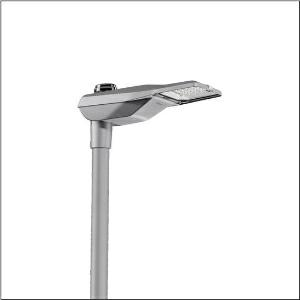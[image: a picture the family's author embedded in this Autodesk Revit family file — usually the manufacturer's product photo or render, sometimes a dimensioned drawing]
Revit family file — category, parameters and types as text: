
# Revit family: streetlight_sl_21_micro___st1_0a_5xe5d27n08db_a8cd
name_source: partatom
category: Lighting Fixtures
units: mm (PartAtom-declared; Revit-internal decimal feet)

## family parameters
Cut with Voids When Loaded = No
Host = Face
Light Source = No
Part Type = Normal
Room Calculation Point = No
Round Connector Dimension = Use Diameter
Shared = No

## types (1)
- --- (1 x LED, 4230 lm, 39.1 W, 2200K)
    Apparent Load = 39 VA
    CIE Flux Codes = 37 72 97 100 100
    Color Rendering = 70
    Color Temperature = 2200K
    Default Elevation = 1800 mm
    Description = Streetlight SL 21 micro, mast luminaire, primary light control with lens, of PMMA, primary optical cover: cover, of toughened safety glass, transparent, light distribution: ST1.0a, light emission: direct distribution, primary light characteristic: asymmetric, installation type: post-top, LED, 3G 1.5mm², High Power LED, rated luminous flux: 4.230lm, luminous efficacy: 108lm/W, light colour: 722, colour temperature: 2200K, control gear: NEMA (7pin), control: overheat protection, pre-setting: linear dimming characteristic, constant luminous flux control, time-dependent luminous flux control, flexible luminous flux parameterisation, mains connection: 230..240V, AC, 50/60Hz, connection cable pre-assembled, cable length: 6,5m, wiring characteristics: H07RN-F, start of lifetime: 39W, end of service life: 41W, reduction: 18W, luminaire housing, of diecast aluminium (EN AC-44300), powder-coated, Siteco® metallic grey (DB 702S), corrosivity category C5 mid according to DIN EN ISO 12944, multi-level sealing system, sealing non-destructively replaceable, inclination adjustable: 0°, 5°, 10°, 15°, length: 528mm, width: 235mm, height: 110mm, spigot size: 76/60mm (post-top), mounting height: 4..8m, protection rating (complete): IP66, insulation class (complete): insulation class I (protective earthing), certification: CE, ENEC, ENEC+, VDE, impact resistance: IK09, permissible operating ambient temperature for outdoor applications: -40..+50°C, standard-compliant lighting for roads and squares, packaging unit: 1 piece

Light Distribution: ST1.0a
    Height = 110 mm
    Lamp = 1 x LED
    Lamp Light Flux = 4230 lm
    Lamp Power = 39.1 W
    Lamp count = 1
    Length = 528 mm
    Luminous efficacy = 108 lm/W
    Manufacturer = Siteco
    ModVariant = No
    Model = 5XE5D27N08DB
    Number of Poles = 1
    OnlyDefault = Yes
    Power Factor = 1
    Product Name = Streetlight SL 21 micro | ST1.0a
    Product group = mast luminaire | pylon top
    ProductGroupID = 6100
    Protection Class = Protection class I
    Protection Degree = IP 66
    RLX_Detail_Level = 1
    RLX_Emergency_Light_Flux = 0 lm
    RLX_Emergency_Type = 0
    RLX_Emergency_Type_DB = No
    RlxData = <blob elided: 98521 chars, md5=0ca2fc9c>
    Socket = socket
    Standby Power = 0 W
    System Light Flux = 4230 lm
    System Power = 39 W
    Type Comments = factory setting: luminous flux: 100 % | dim-lin: 254 | 765 mA
    Type Image = l_1294375.jpg
    URL = http://relux.com
    VarID = @adj_131922
    Voltage = 0 V
    Weight = 0.00 kg
    Width = 235 mm

## geometry (parser evidence)
native form markers: Blend x4, Sweep x10
no freeform markers — native parametric forms only
